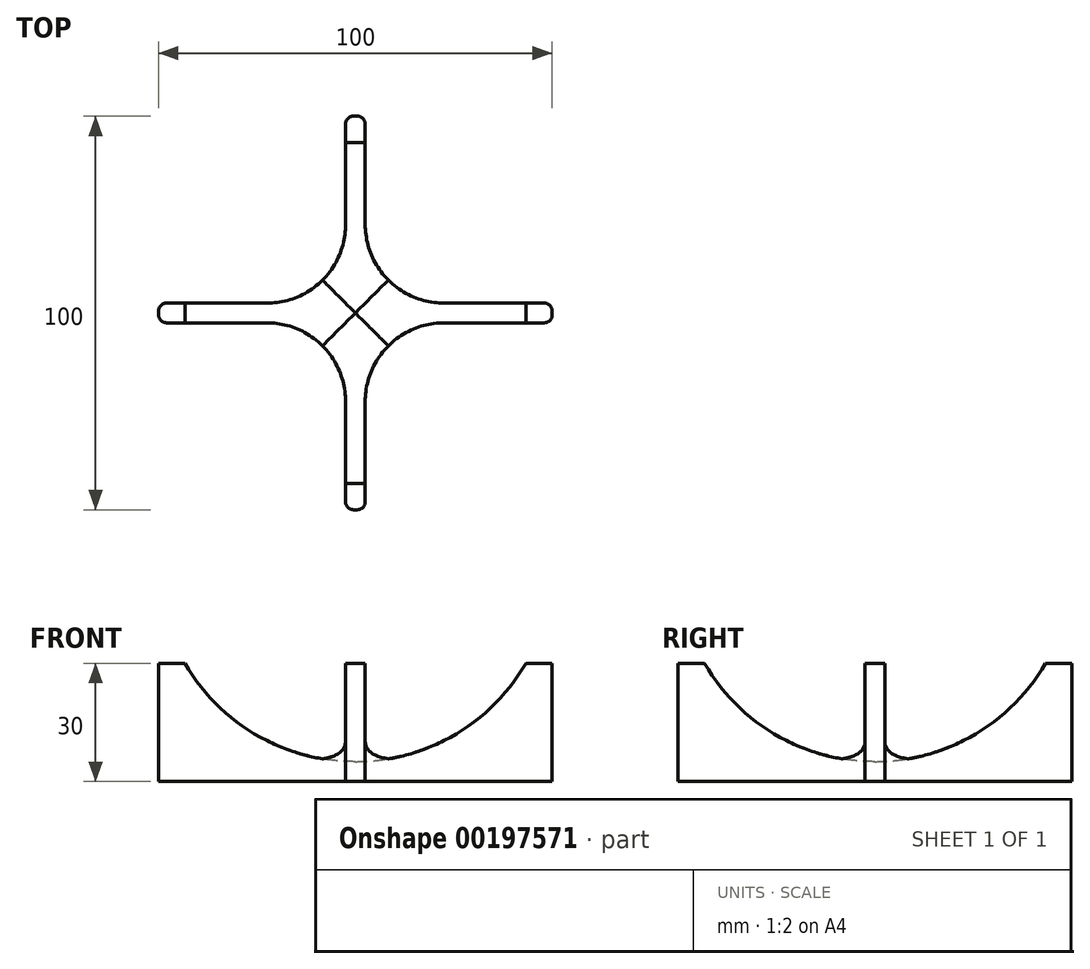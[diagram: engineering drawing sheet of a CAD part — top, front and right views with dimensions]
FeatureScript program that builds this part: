
annotation { "Feature Type Name" : "Feature", "Feature Type Description" : "" }
export const myFeature = defineFeature(function(context is Context, id is Id, definition is map)
    precondition{}
    {
        {
            var Q0;
            Q0=qCreatedBy(makeId("Front.planeOp"),FACE);
            var sketch = newSketch(context, id + "F0", { "sketchPlane" : qUnion([Q0])});
            skLineSegment(sketch, "E0", {"start": v(0, 0) * mm, "end": v(-50, 0) * mm});
            skLineSegment(sketch, "E1", {"start": v(-50, 0) * mm, "end": v(-50, 30) * mm});
            skLineSegment(sketch, "E2", {"start": v(-50, 30) * mm, "end": v(-43.3, 30) * mm});
            skArc(sketch, "E3", {"start": v(-43.3, 30) * mm, "mid": v(-25, 11.7) * mm, "end": v(0, 5) * mm});
            skLineSegment(sketch, "E4", {"start": v(0, 5) * mm, "end": v(0, 0) * mm});
            skSolve(sketch);
        }
        {
            var Q0;
            Q0=makeQuery(id+"F0.imprint","IMPRINT",FACE,{"disambiguationData":[TD([[makeQuery(id+"F0.imprint","IMPRINT",EDGE,{"derivedFrom":sQuery(id+"F0.wireOp",EDGE,"E0")}),-1.0]])]});
            extrude(context, id + "F1", {"entities" : qUnion([Q0]), "endBound" : BoundingType.SYMMETRIC, "depth" : 5 * mm});
        }
        {
            var Q0;
            Q0=makeQuery(id+"F1.opExtrude","SWEPT_FACE",FACE,{"disambiguationData":[OSD([sQuery(id+"F0.wireOp",EDGE,"E4")])]});
            var sketch = newSketch(context, id + "F2", { "sketchPlane" : qUnion([Q0])});
            skLineSegment(sketch, "E5", {"start": v(0, 0) * mm, "end": v(0, 5) * mm, "construction": true});
            skSolve(sketch);
        }
        {
            var Q0;
            Q0=makeQuery(id+"F1.opExtrude","SWEPT_BODY",BODY,{"disambiguationData":[OSD([sQuery(id+"F0.wireOp",EDGE,"E0"),sQuery(id+"F0.wireOp",EDGE,"E1"),sQuery(id+"F0.wireOp",EDGE,"E2"),sQuery(id+"F0.wireOp",EDGE,"E3"),sQuery(id+"F0.wireOp",EDGE,"E4")])]});
            var Q1;
            Q1=sQuery(id+"F2.wireOp",EDGE,"E5");
            circularPattern(context, id + "F3", {"entities" : qUnion([Q0]), "axis" : qUnion([Q1]), "angle" : 360 * degree, "instanceCount" : 4, "equalSpace" : true});
        }
        {
            var Q0;
            Q0=makeQuery(id+"F1.opExtrude","SWEPT_BODY",BODY,{"disambiguationData":[OSD([sQuery(id+"F0.wireOp",EDGE,"E0"),sQuery(id+"F0.wireOp",EDGE,"E1"),sQuery(id+"F0.wireOp",EDGE,"E2"),sQuery(id+"F0.wireOp",EDGE,"E3"),sQuery(id+"F0.wireOp",EDGE,"E4")])]});
            var Q1;
            Q1=makeQuery(id+"F3.opPattern","COPY",BODY,{"derivedFrom":makeQuery(id+"F1.opExtrude","SWEPT_BODY",BODY,{"disambiguationData":[OSD([sQuery(id+"F0.wireOp",EDGE,"E0"),sQuery(id+"F0.wireOp",EDGE,"E1"),sQuery(id+"F0.wireOp",EDGE,"E2"),sQuery(id+"F0.wireOp",EDGE,"E3"),sQuery(id+"F0.wireOp",EDGE,"E4")])]}),"instanceName":"1"});
            var Q2;
            Q2=makeQuery(id+"F3.opPattern","COPY",BODY,{"derivedFrom":makeQuery(id+"F1.opExtrude","SWEPT_BODY",BODY,{"disambiguationData":[OSD([sQuery(id+"F0.wireOp",EDGE,"E0"),sQuery(id+"F0.wireOp",EDGE,"E1"),sQuery(id+"F0.wireOp",EDGE,"E2"),sQuery(id+"F0.wireOp",EDGE,"E3"),sQuery(id+"F0.wireOp",EDGE,"E4")])]}),"instanceName":"3"});
            var Q3;
            Q3=makeQuery(id+"F3.opPattern","COPY",BODY,{"derivedFrom":makeQuery(id+"F1.opExtrude","SWEPT_BODY",BODY,{"disambiguationData":[OSD([sQuery(id+"F0.wireOp",EDGE,"E0"),sQuery(id+"F0.wireOp",EDGE,"E1"),sQuery(id+"F0.wireOp",EDGE,"E2"),sQuery(id+"F0.wireOp",EDGE,"E3"),sQuery(id+"F0.wireOp",EDGE,"E4")])]}),"instanceName":"2"});
            booleanBodies(context, id + "F4", {"operationType" : BooleanOperationType.UNION, "tools" : qUnion([Q0, Q1, Q2, Q3])});
        }
        {
            var Q0;
            {var subQ0=makeQuery(id+"F1.opExtrude","CAP_FACE",FACE,{"disambiguationData":[OSD([sQuery(id+"F0.wireOp",EDGE,"E0"),sQuery(id+"F0.wireOp",EDGE,"E1"),sQuery(id+"F0.wireOp",EDGE,"E2"),sQuery(id+"F0.wireOp",EDGE,"E3"),sQuery(id+"F0.wireOp",EDGE,"E4")])],"isStart":false});Q0=makeQuery(id+"F4.opBoolean","INTERSECT",EDGE,{"derivedFrom":[subQ0,makeQuery(id+"F3.opPattern","COPY",FACE,{"derivedFrom":subQ0,"instanceName":"3"})]});}
            var Q1;
            {var subQ0=sQuery(id+"F0.wireOp",EDGE,"E4");var subQ1=sQuery(id+"F0.wireOp",EDGE,"E3");var subQ2=sQuery(id+"F0.wireOp",EDGE,"E2");var subQ3=sQuery(id+"F0.wireOp",EDGE,"E1");var subQ4=sQuery(id+"F0.wireOp",EDGE,"E0");Q1=makeQuery(id+"F4.opBoolean","INTERSECT",EDGE,{"derivedFrom":[makeQuery(id+"F3.opPattern","COPY",FACE,{"derivedFrom":makeQuery(id+"F1.opExtrude","CAP_FACE",FACE,{"disambiguationData":[OSD([subQ4,subQ3,subQ2,subQ1,subQ0])],"isStart":false}),"instanceName":"1"}),makeQuery(id+"F3.opPattern","COPY",FACE,{"derivedFrom":makeQuery(id+"F1.opExtrude","CAP_FACE",FACE,{"disambiguationData":[OSD([subQ4,subQ3,subQ2,subQ1,subQ0])],"isStart":true}),"instanceName":"2"})]});}
            var Q2;
            {var subQ0=sQuery(id+"F0.wireOp",EDGE,"E4");var subQ1=sQuery(id+"F0.wireOp",EDGE,"E3");var subQ2=sQuery(id+"F0.wireOp",EDGE,"E2");var subQ3=sQuery(id+"F0.wireOp",EDGE,"E1");var subQ4=sQuery(id+"F0.wireOp",EDGE,"E0");Q2=makeQuery(id+"F4.opBoolean","INTERSECT",EDGE,{"derivedFrom":[makeQuery(id+"F3.opPattern","COPY",FACE,{"derivedFrom":makeQuery(id+"F1.opExtrude","CAP_FACE",FACE,{"disambiguationData":[OSD([subQ4,subQ3,subQ2,subQ1,subQ0])],"isStart":false}),"instanceName":"2"}),makeQuery(id+"F3.opPattern","COPY",FACE,{"derivedFrom":makeQuery(id+"F1.opExtrude","CAP_FACE",FACE,{"disambiguationData":[OSD([subQ4,subQ3,subQ2,subQ1,subQ0])],"isStart":true}),"instanceName":"3"})]});}
            var Q3;
            {var subQ0=sQuery(id+"F0.wireOp",EDGE,"E4");var subQ1=sQuery(id+"F0.wireOp",EDGE,"E3");var subQ2=sQuery(id+"F0.wireOp",EDGE,"E2");var subQ3=sQuery(id+"F0.wireOp",EDGE,"E1");var subQ4=sQuery(id+"F0.wireOp",EDGE,"E0");Q3=makeQuery(id+"F4.opBoolean","INTERSECT",EDGE,{"derivedFrom":[makeQuery(id+"F1.opExtrude","CAP_FACE",FACE,{"disambiguationData":[OSD([subQ4,subQ3,subQ2,subQ1,subQ0])],"isStart":true}),makeQuery(id+"F3.opPattern","COPY",FACE,{"derivedFrom":makeQuery(id+"F1.opExtrude","CAP_FACE",FACE,{"disambiguationData":[OSD([subQ4,subQ3,subQ2,subQ1,subQ0])],"isStart":false}),"instanceName":"3"})]});}
            fillet(context, id + "F5", {"entities" : qUnion([Q0, Q1, Q2, Q3]), "radius" : 20 * mm, "tangentPropagation" : true, "allowEdgeOverflow" : false});
        }
        {
            var Q0;
            Q0=makeQuery(id+"F3.opPattern","COPY",EDGE,{"derivedFrom":makeQuery(id+"F1.opExtrude","CAP_EDGE",EDGE,{"disambiguationData":[OSD([sQuery(id+"F0.wireOp",EDGE,"E1")])],"isStart":false}),"instanceName":"3"});
            var Q1;
            Q1=makeQuery(id+"F3.opPattern","COPY",EDGE,{"derivedFrom":makeQuery(id+"F1.opExtrude","CAP_EDGE",EDGE,{"disambiguationData":[OSD([sQuery(id+"F0.wireOp",EDGE,"E1")])],"isStart":true}),"instanceName":"3"});
            var Q2;
            Q2=makeQuery(id+"F1.opExtrude","CAP_EDGE",EDGE,{"disambiguationData":[OSD([sQuery(id+"F0.wireOp",EDGE,"E1")])],"isStart":true});
            var Q3;
            Q3=makeQuery(id+"F1.opExtrude","CAP_EDGE",EDGE,{"disambiguationData":[OSD([sQuery(id+"F0.wireOp",EDGE,"E1")])],"isStart":false});
            var Q4;
            Q4=makeQuery(id+"F3.opPattern","COPY",EDGE,{"derivedFrom":makeQuery(id+"F1.opExtrude","CAP_EDGE",EDGE,{"disambiguationData":[OSD([sQuery(id+"F0.wireOp",EDGE,"E1")])],"isStart":true}),"instanceName":"1"});
            var Q5;
            Q5=makeQuery(id+"F3.opPattern","COPY",EDGE,{"derivedFrom":makeQuery(id+"F1.opExtrude","CAP_EDGE",EDGE,{"disambiguationData":[OSD([sQuery(id+"F0.wireOp",EDGE,"E1")])],"isStart":false}),"instanceName":"1"});
            var Q6;
            Q6=makeQuery(id+"F3.opPattern","COPY",EDGE,{"derivedFrom":makeQuery(id+"F1.opExtrude","CAP_EDGE",EDGE,{"disambiguationData":[OSD([sQuery(id+"F0.wireOp",EDGE,"E1")])],"isStart":true}),"instanceName":"2"});
            var Q7;
            Q7=makeQuery(id+"F3.opPattern","COPY",EDGE,{"derivedFrom":makeQuery(id+"F1.opExtrude","CAP_EDGE",EDGE,{"disambiguationData":[OSD([sQuery(id+"F0.wireOp",EDGE,"E1")])],"isStart":false}),"instanceName":"2"});
            fillet(context, id + "F6", {"entities" : qUnion([Q0, Q1, Q2, Q3, Q4, Q5, Q6, Q7]), "radius" : 2 * mm, "tangentPropagation" : true, "allowEdgeOverflow" : false});
        }
    });
